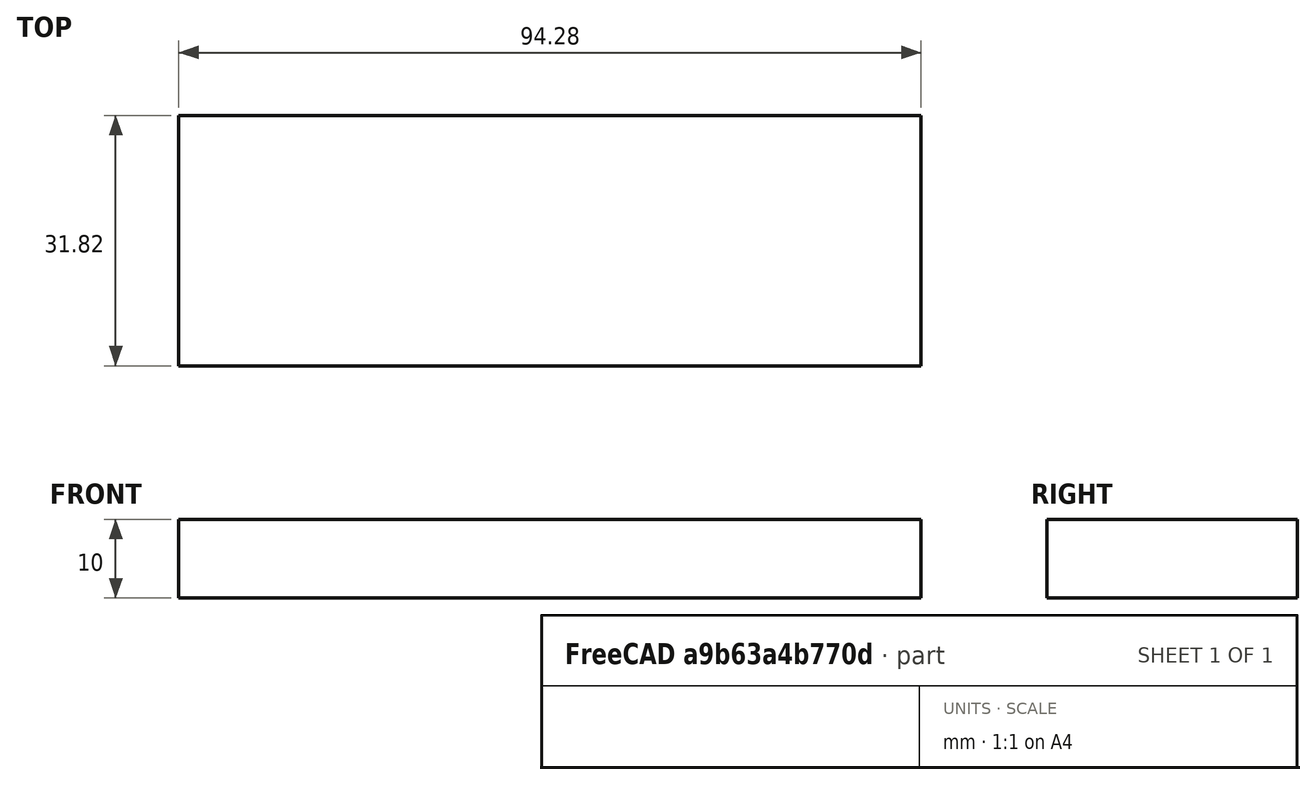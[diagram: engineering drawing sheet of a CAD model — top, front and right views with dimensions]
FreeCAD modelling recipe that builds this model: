
FCSTD DOCUMENT  (FreeCAD 0.21R33771 (Git))
Label: bateria
License: All rights reserved
LicenseURL: http://en.wikipedia.org/wiki/All_rights_reserved
objects: Sketcher::SketchObject×2, PartDesign::Body×2, PartDesign::Pad×1, PartDesign::ShapeBinder×1
note: 7 computed .brp shape members not serialized (recipe doc carries the construction recipe); baked Part::Feature solids carry a one-line shape summary decoded from their .brp

FEATURE [Sketcher::SketchObject] Sketch
  FullyConstrained = false
  MapMode = 5
  Support = -> [XY_Plane]
  sketch-geometry (4):
    g0: LineSegment StartX=-46.0113 StartY=15.5052 StartZ=0 EndX=48.2699 EndY=15.5052 EndZ=0
    g1: LineSegment StartX=48.2699 StartY=15.5052 StartZ=0 EndX=48.2699 EndY=-16.3129 EndZ=0
    g2: LineSegment StartX=48.2699 StartY=-16.3129 StartZ=0 EndX=-46.0113 EndY=-16.3129 EndZ=0
    g3: LineSegment StartX=-46.0113 StartY=-16.3129 StartZ=0 EndX=-46.0113 EndY=15.5052 EndZ=0
  constraints (8):
    c: Coincident(g0,g1)
    c: Coincident(g1,g2)
    c: Coincident(g2,g3)
    c: Coincident(g3,g0)
    c: Horizontal(g0)
    c: Horizontal(g2)
    c: Vertical(g1)
    c: Vertical(g3)
FEATURE [PartDesign::Pad] Pad
  Direction = (0,0,1)
  Length = 10
  Length2 = 10
  Profile = -> Sketch
  ReferenceAxis = -> Sketch [N_Axis]
  Type = 0
FEATURE [PartDesign::Body] Body
  Group = -> [Sketch,Pad]
  Origin = -> Origin
  Tip = -> Pad
FEATURE [PartDesign::ShapeBinder] ShapeBinder
  Support = -> [Pad]
  TraceSupport = false
FEATURE [Sketcher::SketchObject] Sketch001
  FullyConstrained = true
  MapMode = 5
  Placement = pos=(0,0,0) rot=(1,0,0;3.14159rad)
  Support = -> [ShapeBinder]
FEATURE [PartDesign::Body] Body001
  Group = -> [ShapeBinder,Sketch001]
  Origin = -> Origin001
